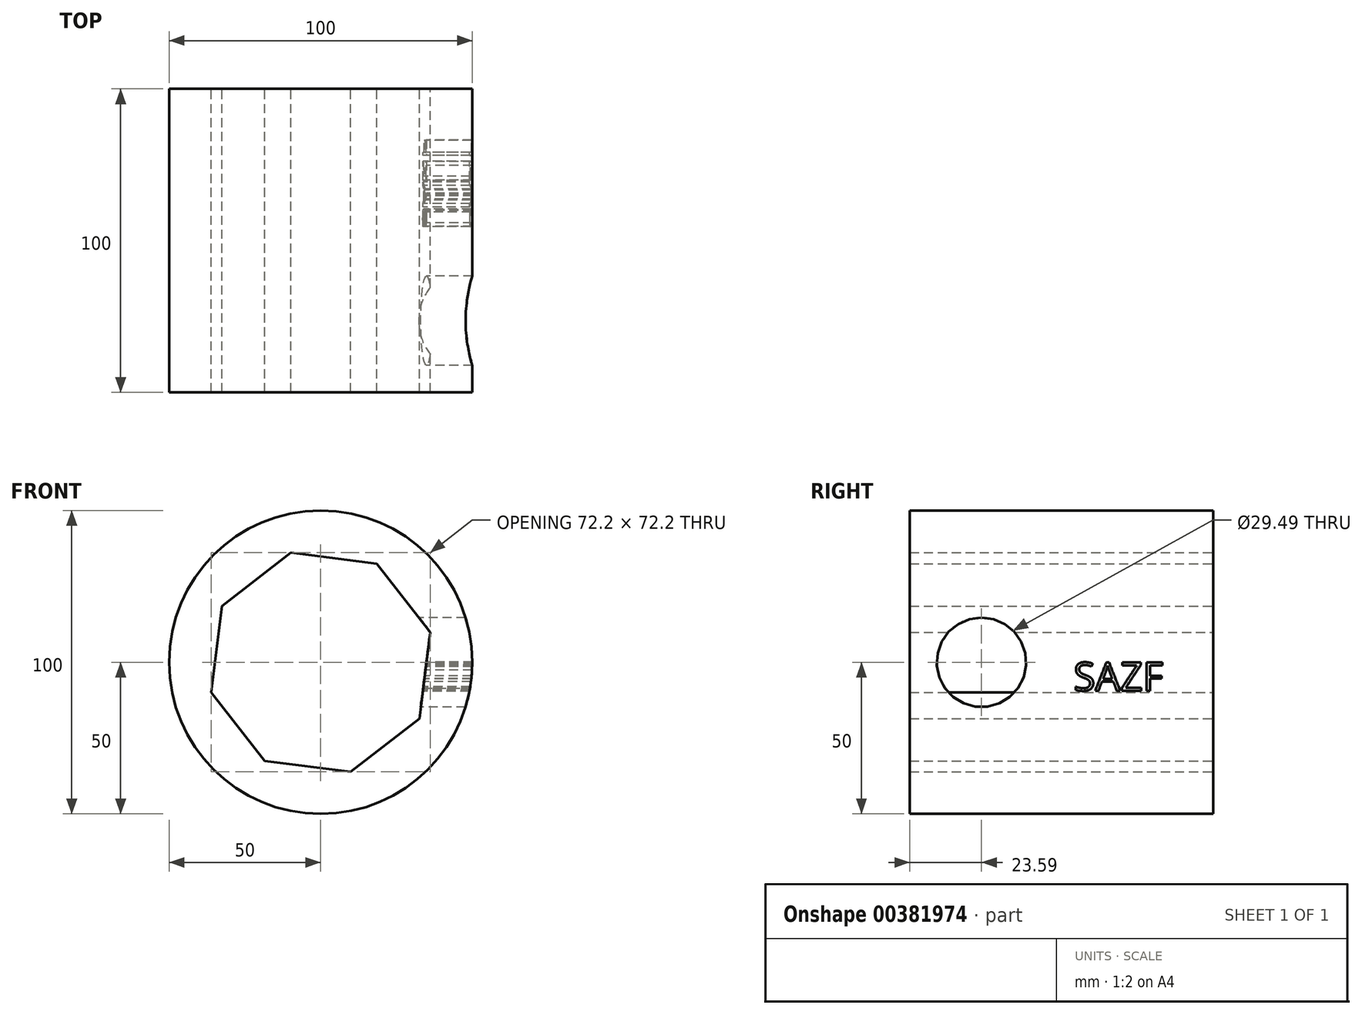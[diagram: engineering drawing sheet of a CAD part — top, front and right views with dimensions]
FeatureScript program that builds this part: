
annotation { "Feature Type Name" : "Feature", "Feature Type Description" : "" }
export const myFeature = defineFeature(function(context is Context, id is Id, definition is map)
    precondition{}
    {
        {
            var Q0;
            Q0=qCreatedBy(makeId("Front.planeOp"),FACE);
            var sketch = newSketch(context, id + "F0", { "sketchPlane" : qUnion([Q0])});
            skCircle(sketch, "E0", {"center": v(0, 0) * mm, "radius": 50 * mm});
            skSolve(sketch);
        }
        {
            var Q0;
            Q0=makeQuery(id+"F0.imprint","IMPRINT",FACE,{"disambiguationData":[TD([[makeQuery(id+"F0.imprint","IMPRINT",EDGE,{"derivedFrom":sQuery(id+"F0.wireOp",EDGE,"E0")}),1.0]])]});
            extrude(context, id + "F1", {"entities" : qUnion([Q0]), "depth" : 100 * mm});
        }
        {
            var Q0;
            Q0=qCreatedBy(makeId("Front.planeOp"),FACE);
            var sketch = newSketch(context, id + "F2", { "sketchPlane" : qUnion([Q0])});
            skCircle(sketch, "E1.cCircle", {"center": v(0, 0) * mm, "radius": 34.58 * mm, "construction": true});
            skLineSegment(sketch, "E1.0", {"start": v(18.53, 32.53) * mm, "end": v(36.1, 9.9) * mm});
            skLineSegment(sketch, "E1.1", {"start": v(36.1, 9.9) * mm, "end": v(32.53, -18.53) * mm});
            skLineSegment(sketch, "E1.2", {"start": v(32.53, -18.53) * mm, "end": v(9.9, -36.1) * mm});
            skLineSegment(sketch, "E1.3", {"start": v(9.9, -36.1) * mm, "end": v(-18.53, -32.53) * mm});
            skLineSegment(sketch, "E1.4", {"start": v(-18.53, -32.53) * mm, "end": v(-36.1, -9.9) * mm});
            skLineSegment(sketch, "E1.5", {"start": v(-36.1, -9.9) * mm, "end": v(-32.53, 18.53) * mm});
            skLineSegment(sketch, "E1.6", {"start": v(-32.53, 18.53) * mm, "end": v(-9.9, 36.1) * mm});
            skLineSegment(sketch, "E1.7", {"start": v(-9.9, 36.1) * mm, "end": v(18.53, 32.53) * mm});
            skPoint(sketch, "E1.0.midPoint", {"position": v(27.31, 21.21) * mm});
            skSolve(sketch);
        }
        {
            var Q0;
            Q0 = qSketchRegion(id + "F2", true);
            extrude(context, id + "F3", {"entities" : qUnion([Q0]), "operationType" : NewBodyOperationType.REMOVE, "endBound" : BoundingType.THROUGH_ALL, "depth" : 62.7 * mm});
        }
        {
            var Q0;
            Q0=qCreatedBy(makeId("Right.planeOp"),FACE);
            var sketch = newSketch(context, id + "F4", { "sketchPlane" : qUnion([Q0])});
            skCircle(sketch, "E2", {"center": v(-76.41, 0) * mm, "radius": 14.75 * mm});
            skSolve(sketch);
        }
        {
            var Q0;
            Q0=makeQuery(id+"F4.imprint","IMPRINT",FACE,{"disambiguationData":[TD([[makeQuery(id+"F4.imprint","IMPRINT",EDGE,{"derivedFrom":sQuery(id+"F4.wireOp",EDGE,"E2")}),1.0]])]});
            var Q1;
            Q1=sQuery(id+"F4.wireOp",EDGE,"E2");
            extrude(context, id + "F5", {"entities" : qUnion([Q0]), "operationType" : NewBodyOperationType.REMOVE, "surfaceEntities" : qUnion([Q1]), "depth" : 69.6 * mm});
        }
        {
            var Q0;
            Q0=qCreatedBy(makeId("Right.planeOp"),FACE);
            var sketch = newSketch(context, id + "F6", { "sketchPlane" : qUnion([Q0])});
            skText(sketch, "E3", { "text": "SAZF", "fontName": "OpenSans-Regular.ttf"});
            const initialGuessF6  = {"E3": [-0.04606, -0.00938, 1, 0, 0.00938]};
            skSetInitialGuess(sketch, initialGuessF6);
            skSolve(sketch);
        }
        {
            var Q0;
            Q0 = qSketchRegion(id + "F6", true);
            extrude(context, id + "F7", {"entities" : qUnion([Q0]), "operationType" : NewBodyOperationType.REMOVE, "depth" : 76.7 * mm});
        }
    });
